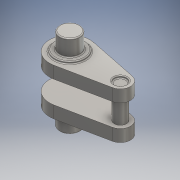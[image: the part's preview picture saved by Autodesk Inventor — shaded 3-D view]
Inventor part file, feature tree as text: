
AUTODESK INVENTOR PART (.ipt)
format: ipt  version: 2016 (Build 200138000, 138)  size: 212,992 bytes
history: native  units: mm
features: extrude x4, sketch x4, projected_geometry x3, plane x1, fillet x1, mirror x1
ambient origin geometry x8: Origin, YZ Plane, XZ Plane, XY Plane, X Axis, Y Axis, Z Axis, Center Point
bodies: Solid1 (feature_tree)
feature tree (14):
  extrude  "Extrusion1"  Depth=21.0mm TaperAngle=0.0deg
  plane  "Work Plane1"
  extrude  "Extrusion2"  Depth=20.0mm
  extrude  "Extrusion3"  Depth=50.0mm
  extrude  "Extrusion4"  Depth=30.0mm
  fillet  "Fillet1"  Radius=2.0mm
  mirror  "Mirror1"
  sketch  "Sketch1"  dims[d0=12.0mm d1=21.0mm d2=0.0mm]
  sketch  "Sketch2"  dims[d3=-10.0mm d4=20.0mm]
  projected_geometry  "Projected Loop1"
  sketch  "Sketch3"  dims[d5=40.0mm d6=50.0mm]
  projected_geometry  "Projected Loop2"
  sketch  "Sketch4"  dims[d7=12.0mm d8=0.0mm d9=30.0mm d10=2.0mm d11=0.0mm d12=20.0mm d13=16.0mm d14=0.0mm d15=1.0mm]
  projected_geometry  "Projected Loop3"
